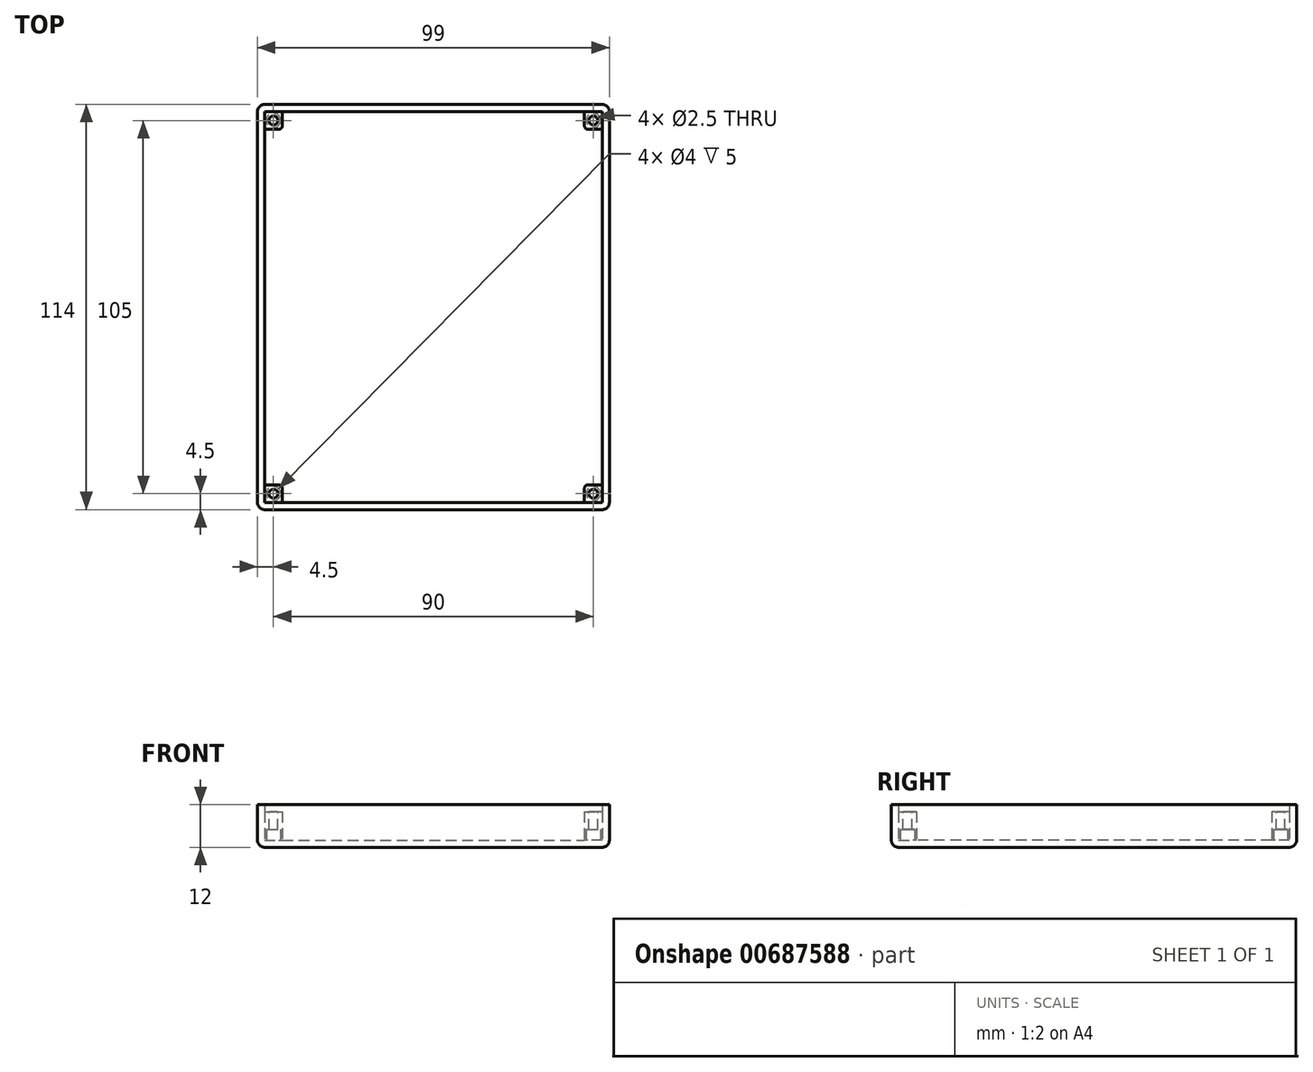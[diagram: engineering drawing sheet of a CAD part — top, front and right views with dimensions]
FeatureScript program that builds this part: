
annotation { "Feature Type Name" : "Feature", "Feature Type Description" : "" }
export const myFeature = defineFeature(function(context is Context, id is Id, definition is map)
    precondition{}
    {
        {
            var Q0;
            Q0=qCreatedBy(makeId("Top.planeOp"),FACE);
            var sketch = newSketch(context, id + "F0", { "sketchPlane" : qUnion([Q0])});
            skLineSegment(sketch, "E0.bottom", {"start": v(-47.5, 55) * mm, "end": v(47.5, 55) * mm});
            skLineSegment(sketch, "E0.top", {"start": v(-47.5, -55) * mm, "end": v(47.5, -55) * mm});
            skLineSegment(sketch, "E0.left", {"start": v(-47.5, 55) * mm, "end": v(-47.5, -55) * mm});
            skLineSegment(sketch, "E0.right", {"start": v(47.5, 55) * mm, "end": v(47.5, -55) * mm});
            skPoint(sketch, "E0.middle", {"position": v(0, 0) * mm});
            skSolve(sketch);
        }
        {
            var Q0;
            Q0=makeQuery(id+"F0.imprint","IMPRINT",FACE,{"disambiguationData":[TD([[makeQuery(id+"F0.imprint","IMPRINT",EDGE,{"derivedFrom":sQuery(id+"F0.wireOp",EDGE,"E0.bottom")}),-1.0]])]});
            extrude(context, id + "F1", {"entities" : qUnion([Q0]), "depth" : 10 * mm, "offsetDistance" : 25 * mm});
        }
        {
            var Q0;
            Q0=makeQuery(id+"F1.opExtrude","CAP_FACE",FACE,{"disambiguationData":[OSD([sQuery(id+"F0.wireOp",EDGE,"E0.bottom"),sQuery(id+"F0.wireOp",EDGE,"E0.top"),sQuery(id+"F0.wireOp",EDGE,"E0.left"),sQuery(id+"F0.wireOp",EDGE,"E0.right")])],"isStart":false});
            shell(context, id + "F2", {"entities" : qUnion([Q0]), "thickness" : 2 * mm, "oppositeDirection" : true});
        }
        {
            var Q0;
            Q0=makeQuery(id+"F1.opExtrude","CAP_EDGE",EDGE,{"disambiguationData":[OSD([sQuery(id+"F0.wireOp",EDGE,"E0.top")])],"isStart":true});
            var Q1;
            Q1=makeQuery(id+"F1.opExtrude","CAP_FACE",FACE,{"disambiguationData":[OSD([sQuery(id+"F0.wireOp",EDGE,"E0.bottom"),sQuery(id+"F0.wireOp",EDGE,"E0.top"),sQuery(id+"F0.wireOp",EDGE,"E0.left"),sQuery(id+"F0.wireOp",EDGE,"E0.right")])],"isStart":true});
            var Q2;
            Q2=makeQuery(id+"F1.opExtrude","SWEPT_EDGE",EDGE,{"disambiguationData":[OSD([sQuery(id+"F0.wireOp",EDGE,"E0.top"),sQuery(id+"F0.wireOp",EDGE,"E0.left")])]});
            var Q3;
            Q3=makeQuery(id+"F1.opExtrude","SWEPT_EDGE",EDGE,{"disambiguationData":[OSD([sQuery(id+"F0.wireOp",EDGE,"E0.bottom"),sQuery(id+"F0.wireOp",EDGE,"E0.left")])]});
            var Q4;
            Q4=makeQuery(id+"F1.opExtrude","SWEPT_EDGE",EDGE,{"disambiguationData":[OSD([sQuery(id+"F0.wireOp",EDGE,"E0.bottom"),sQuery(id+"F0.wireOp",EDGE,"E0.right")])]});
            var Q5;
            Q5=makeQuery(id+"F1.opExtrude","SWEPT_EDGE",EDGE,{"disambiguationData":[OSD([sQuery(id+"F0.wireOp",EDGE,"E0.top"),sQuery(id+"F0.wireOp",EDGE,"E0.right")])]});
            fillet(context, id + "F3", {"entities" : qUnion([Q0, Q1, Q2, Q3, Q4, Q5]), "radius" : 2 * mm, "tangentPropagation" : true, "allowEdgeOverflow" : false});
        }
        {
            var Q0;
            Q0=makeQuery(id+"F2.opShell","OFFSET_FACE",FACE,{"disambiguationData":[OSD([sQuery(id+"F0.wireOp",EDGE,"E0.bottom"),sQuery(id+"F0.wireOp",EDGE,"E0.top"),sQuery(id+"F0.wireOp",EDGE,"E0.left"),sQuery(id+"F0.wireOp",EDGE,"E0.right")])]});
            var sketch = newSketch(context, id + "F4", { "sketchPlane" : qUnion([Q0])});
            skLineSegment(sketch, "E1.bottom", {"start": v(47.5, 55) * mm, "end": v(42.5, 55) * mm});
            skLineSegment(sketch, "E1.top", {"start": v(47.5, 50) * mm, "end": v(42.5, 50) * mm});
            skLineSegment(sketch, "E1.left", {"start": v(47.5, 55) * mm, "end": v(47.5, 50) * mm});
            skLineSegment(sketch, "E1.right", {"start": v(42.5, 55) * mm, "end": v(42.5, 50) * mm});
            skLineSegment(sketch, "E2.bottom", {"start": v(-47.5, 55) * mm, "end": v(-42.5, 55) * mm});
            skLineSegment(sketch, "E2.top", {"start": v(-47.5, 50) * mm, "end": v(-42.5, 50) * mm});
            skLineSegment(sketch, "E2.left", {"start": v(-47.5, 55) * mm, "end": v(-47.5, 50) * mm});
            skLineSegment(sketch, "E2.right", {"start": v(-42.5, 55) * mm, "end": v(-42.5, 50) * mm});
            skLineSegment(sketch, "E3.bottom", {"start": v(-47.5, -55) * mm, "end": v(-42.5, -55) * mm});
            skLineSegment(sketch, "E3.top", {"start": v(-47.5, -50) * mm, "end": v(-42.5, -50) * mm});
            skLineSegment(sketch, "E3.left", {"start": v(-47.5, -55) * mm, "end": v(-47.5, -50) * mm});
            skLineSegment(sketch, "E3.right", {"start": v(-42.5, -55) * mm, "end": v(-42.5, -50) * mm});
            skLineSegment(sketch, "E4.bottom", {"start": v(47.5, -55) * mm, "end": v(42.5, -55) * mm});
            skLineSegment(sketch, "E4.top", {"start": v(47.5, -50) * mm, "end": v(42.5, -50) * mm});
            skLineSegment(sketch, "E4.left", {"start": v(47.5, -55) * mm, "end": v(47.5, -50) * mm});
            skLineSegment(sketch, "E4.right", {"start": v(42.5, -55) * mm, "end": v(42.5, -50) * mm});
            skSolve(sketch);
        }
        {
            var Q0;
            Q0=makeQuery(id+"F4.imprint","IMPRINT",FACE,{"disambiguationData":[TD([[makeQuery(id+"F4.imprint","IMPRINT",EDGE,{"derivedFrom":sQuery(id+"F4.wireOp",EDGE,"E2.bottom")}),-1.0]])]});
            var Q1;
            Q1=makeQuery(id+"F4.imprint","IMPRINT",FACE,{"disambiguationData":[TD([[makeQuery(id+"F4.imprint","IMPRINT",EDGE,{"derivedFrom":sQuery(id+"F4.wireOp",EDGE,"E1.bottom")}),-1.0]])]});
            var Q2;
            Q2=makeQuery(id+"F4.imprint","IMPRINT",FACE,{"disambiguationData":[TD([[makeQuery(id+"F4.imprint","IMPRINT",EDGE,{"derivedFrom":sQuery(id+"F4.wireOp",EDGE,"E4.bottom")}),1.0]])]});
            var Q3;
            Q3=makeQuery(id+"F4.imprint","IMPRINT",FACE,{"disambiguationData":[TD([[makeQuery(id+"F4.imprint","IMPRINT",EDGE,{"derivedFrom":sQuery(id+"F4.wireOp",EDGE,"E3.bottom")}),1.0]])]});
            extrude(context, id + "F5", {"entities" : qUnion([Q0, Q1, Q2, Q3]), "operationType" : NewBodyOperationType.ADD, "depth" : 8 * mm, "offsetDistance" : 25 * mm});
        }
        {
            var Q0;
            Q0=makeQuery(id+"F5.opExtrude","SWEPT_EDGE",EDGE,{"disambiguationData":[OSD([sQuery(id+"F0.wireOp",EDGE,"E0.left"),sQuery(id+"F4.wireOp",EDGE,"E2.top"),sQuery(id+"F4.wireOp",EDGE,"E2.left")])]});
            var Q1;
            Q1=makeQuery(id+"F5.opExtrude","SWEPT_EDGE",EDGE,{"disambiguationData":[OSD([sQuery(id+"F4.wireOp",EDGE,"E2.top"),sQuery(id+"F4.wireOp",EDGE,"E2.right")])]});
            var Q2;
            Q2=makeQuery(id+"F5.opExtrude","SWEPT_EDGE",EDGE,{"disambiguationData":[OSD([sQuery(id+"F0.wireOp",EDGE,"E0.bottom"),sQuery(id+"F4.wireOp",EDGE,"E2.bottom"),sQuery(id+"F4.wireOp",EDGE,"E2.right")])]});
            var Q3;
            Q3=makeQuery(id+"F5.opExtrude","SWEPT_EDGE",EDGE,{"disambiguationData":[OSD([sQuery(id+"F0.wireOp",EDGE,"E0.bottom"),sQuery(id+"F4.wireOp",EDGE,"E1.bottom"),sQuery(id+"F4.wireOp",EDGE,"E1.right")])]});
            var Q4;
            Q4=makeQuery(id+"F5.opExtrude","SWEPT_EDGE",EDGE,{"disambiguationData":[OSD([sQuery(id+"F4.wireOp",EDGE,"E1.top"),sQuery(id+"F4.wireOp",EDGE,"E1.right")])]});
            var Q5;
            Q5=makeQuery(id+"F5.opExtrude","SWEPT_EDGE",EDGE,{"disambiguationData":[OSD([sQuery(id+"F0.wireOp",EDGE,"E0.right"),sQuery(id+"F4.wireOp",EDGE,"E1.top"),sQuery(id+"F4.wireOp",EDGE,"E1.left")])]});
            var Q6;
            Q6=makeQuery(id+"F5.opExtrude","SWEPT_EDGE",EDGE,{"disambiguationData":[OSD([sQuery(id+"F0.wireOp",EDGE,"E0.top"),sQuery(id+"F4.wireOp",EDGE,"E3.bottom"),sQuery(id+"F4.wireOp",EDGE,"E3.right")])]});
            var Q7;
            Q7=makeQuery(id+"F5.opExtrude","SWEPT_EDGE",EDGE,{"disambiguationData":[OSD([sQuery(id+"F4.wireOp",EDGE,"E3.top"),sQuery(id+"F4.wireOp",EDGE,"E3.right")])]});
            var Q8;
            Q8=makeQuery(id+"F5.opExtrude","SWEPT_EDGE",EDGE,{"disambiguationData":[OSD([sQuery(id+"F0.wireOp",EDGE,"E0.left"),sQuery(id+"F4.wireOp",EDGE,"E3.top"),sQuery(id+"F4.wireOp",EDGE,"E3.left")])]});
            var Q9;
            Q9=makeQuery(id+"F5.opExtrude","SWEPT_EDGE",EDGE,{"disambiguationData":[OSD([sQuery(id+"F0.wireOp",EDGE,"E0.top"),sQuery(id+"F4.wireOp",EDGE,"E4.bottom"),sQuery(id+"F4.wireOp",EDGE,"E4.right")])]});
            var Q10;
            Q10=makeQuery(id+"F5.opExtrude","SWEPT_EDGE",EDGE,{"disambiguationData":[OSD([sQuery(id+"F4.wireOp",EDGE,"E4.top"),sQuery(id+"F4.wireOp",EDGE,"E4.right")])]});
            var Q11;
            Q11=makeQuery(id+"F5.opExtrude","SWEPT_EDGE",EDGE,{"disambiguationData":[OSD([sQuery(id+"F0.wireOp",EDGE,"E0.right"),sQuery(id+"F4.wireOp",EDGE,"E4.top"),sQuery(id+"F4.wireOp",EDGE,"E4.left")])]});
            fillet(context, id + "F6", {"entities" : qUnion([Q0, Q1, Q2, Q3, Q4, Q5, Q6, Q7, Q8, Q9, Q10, Q11]), "radius" : 1 * mm, "tangentPropagation" : true, "allowEdgeOverflow" : false});
        }
        {
            var Q0;
            Q0=makeQuery(id+"F5.opExtrude","CAP_FACE",FACE,{"disambiguationData":[OSD([sQuery(id+"F4.wireOp",EDGE,"E2.bottom"),sQuery(id+"F4.wireOp",EDGE,"E2.top"),sQuery(id+"F4.wireOp",EDGE,"E2.left"),sQuery(id+"F4.wireOp",EDGE,"E2.right")])],"isStart":false});
            var sketch = newSketch(context, id + "F7", { "sketchPlane" : qUnion([Q0])});
            skCircle(sketch, "E5", {"center": v(-45, -52.5) * mm, "radius": 1.25 * mm});
            skPoint(sketch, "E5.centerSnap0", {"position": v(-45, -50) * mm});
            skPoint(sketch, "E5.centerSnap1", {"position": v(-42.5, -52.5) * mm});
            skCircle(sketch, "E6", {"center": v(45, -52.5) * mm, "radius": 1.25 * mm});
            skPoint(sketch, "E6.centerSnap0", {"position": v(45, -50) * mm});
            skPoint(sketch, "E6.centerSnap1", {"position": v(42.5, -52.5) * mm});
            skCircle(sketch, "E7", {"center": v(45, 52.5) * mm, "radius": 1.25 * mm});
            skPoint(sketch, "E7.centerSnap0", {"position": v(45, 50) * mm});
            skPoint(sketch, "E7.centerSnap1", {"position": v(42.5, 52.5) * mm});
            skCircle(sketch, "E8", {"center": v(-45, 52.5) * mm, "radius": 1.25 * mm});
            skPoint(sketch, "E8.centerSnap0", {"position": v(-45, 50) * mm});
            skPoint(sketch, "E8.centerSnap1", {"position": v(-42.5, 52.5) * mm});
            skSolve(sketch);
        }
        {
            var Q0;
            Q0=qSketchRegion(id+"F7",true);
            extrude(context, id + "F8", {"entities" : qUnion([Q0]), "operationType" : NewBodyOperationType.REMOVE, "endBound" : BoundingType.UP_TO_NEXT, "oppositeDirection" : true, "depth" : 25 * mm, "offsetDistance" : 25 * mm});
        }
        {
            var Q0;
            Q0=makeQuery(id+"F1.opExtrude","CAP_FACE",FACE,{"disambiguationData":[OSD([sQuery(id+"F0.wireOp",EDGE,"E0.bottom"),sQuery(id+"F0.wireOp",EDGE,"E0.top"),sQuery(id+"F0.wireOp",EDGE,"E0.left"),sQuery(id+"F0.wireOp",EDGE,"E0.right")])],"isStart":true});
            var sketch = newSketch(context, id + "F9", { "sketchPlane" : qUnion([Q0])});
            skCircle(sketch, "E9", {"center": v(-45, -52.5) * mm, "radius": 2 * mm});
            skCircle(sketch, "E10", {"center": v(45, -52.5) * mm, "radius": 2 * mm});
            skCircle(sketch, "E11", {"center": v(45, 52.5) * mm, "radius": 2 * mm});
            skCircle(sketch, "E12", {"center": v(-45, 52.5) * mm, "radius": 2 * mm});
            skSolve(sketch);
        }
        {
            var Q0;
            Q0=qSketchRegion(id+"F9",true);
            extrude(context, id + "F10", {"entities" : qUnion([Q0]), "operationType" : NewBodyOperationType.REMOVE, "oppositeDirection" : true, "depth" : 5 * mm, "offsetDistance" : 25 * mm});
        }
    });
